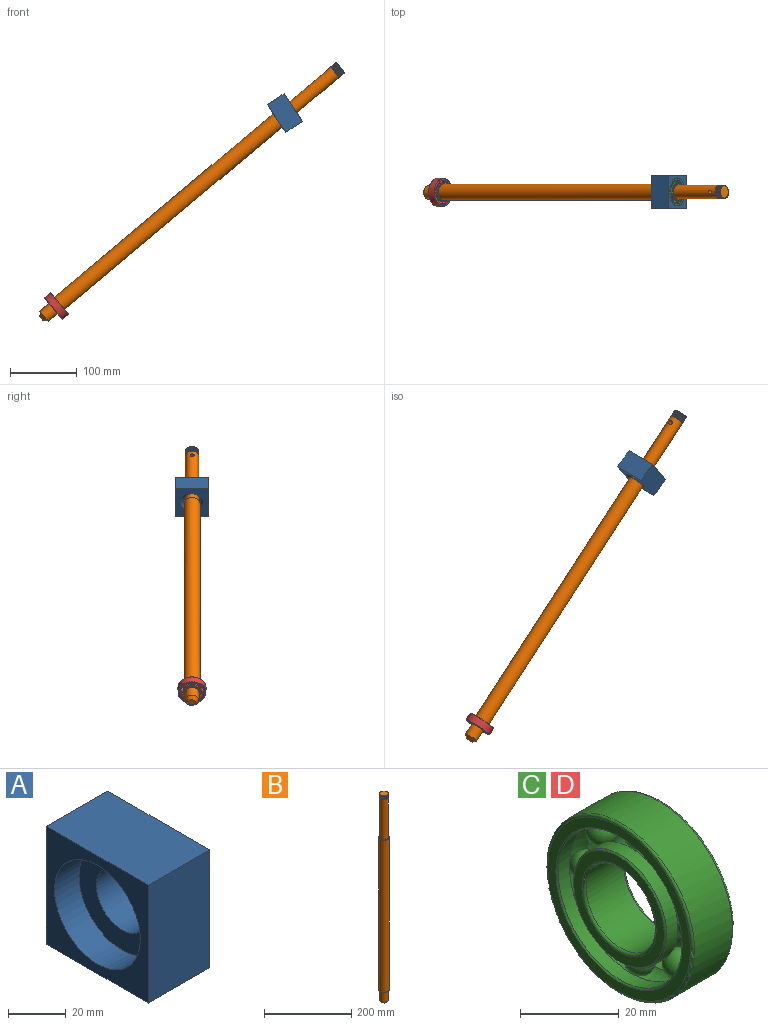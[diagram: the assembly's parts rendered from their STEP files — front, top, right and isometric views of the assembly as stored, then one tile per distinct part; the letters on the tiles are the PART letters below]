
ASSEMBLY  parts=4 mates=1
PART A: 10 faces, bbox 30x50x50 mm
  f0: plane 50x50mm, normal (-1,0,0), area 1114.6mm2, adj f1,f3,f4,f5,f8
  f1: plane 50x30mm, normal (0,-1,0), area 1500mm2, adj f0,f2,f4,f5
  f2: plane 50x50mm, normal (1,0,0), area 1537.9mm2, adj f1,f3,f4,f5,f9
  f3: plane 50x30mm, normal (0,1,0), area 1500mm2, adj f0,f2,f4,f5
  f4: plane 50x30mm, normal (0,0,1), area 1500mm2, adj f0,f1,f2,f3
  f5: plane 50x30mm, normal (0,0,-1), area 1500mm2, adj f0,f1,f2,f3
  f6: cylinder r=12.5mm len=25mm, axis (-1,0,0), area 1021mm2, adj f7,f9
  f7: plane 42x42mm, normal (-1,0,0), area 894.6mm2, adj f6,f8
  f8: cylinder r=21mm len=42mm, axis (-1,0,0), area 1583.4mm2, adj f0,f7
  f9: cone r=17.5mm half-angle=45deg, axis (1,0,0), area 666.4mm2, adj f2,f6
PART B: 27 faces, bbox 27.7x27.7x589.1 mm
  f0: plane 24x24mm, normal (0,0,-1), area 138.2mm2, adj f1,f2
  f1: cylinder r=10mm len=30mm, axis (0,0,-1), area 1885mm2, adj f0,f4
  f2: cylinder r=12mm len=427.31mm, axis (0,0,-1), area 32167.7mm2, adj f0,f5
  f3: plane 10x10mm, normal (0,0,-1), area 78.5mm2, adj f4
  f4: cone r=10mm half-angle=45deg, axis (0,0,1), area 333.2mm2, adj f1,f3
  f5: plane 27.66x27.66mm, normal (0,-0.11,0.99), area 139.1mm2, adj f2,f7
  f6: plane 19.73x19.68mm, normal (0,0,1), area 294.9mm2, adj f17,f21,f22,f23
  f7: cylinder r=10mm len=114.81mm, axis (0,0,-1), area 7046.2mm2, adj f5,f8,f18,f19,f20,f23,f25
  f8: cylinder r=10mm len=20mm, axis (0,0,-1), area 7.8mm2, adj f7,f9,f22,f23
  f9: cylinder r=10mm len=20mm, axis (0,0,-1), area 7.8mm2, adj f8,f10,f22,f23
  f10: cylinder r=10mm len=20mm, axis (0,0,-1), area 7.9mm2, adj f9,f11,f22,f23
  f11: cylinder r=10mm len=20mm, axis (0,0,-1), area 7.9mm2, adj f10,f12,f22,f23
  f12: cylinder r=10mm len=20mm, axis (0,0,-1), area 7.8mm2, adj f11,f13,f22,f23
  f13: cylinder r=10mm len=20mm, axis (0,0,-1), area 7.8mm2, adj f12,f14,f22,f23
  f14: cylinder r=10mm len=20mm, axis (0,0,-1), area 7.9mm2, adj f13,f15,f22,f23
  f15: cylinder r=10mm len=20mm, axis (0,0,-1), area 7.9mm2, adj f14,f16,f22,f23
  f16: cylinder r=10mm len=20mm, axis (0,0,-1), area 7.9mm2, adj f15,f17,f22,f23
  f17: cylinder r=10mm len=7.01mm, axis (0,0,-1), area 0.5mm2, adj f6,f16,f22
  f18: plane 0.3x0.1mm, normal (0,-1,0), area 0mm2, adj f7,f19,f20,f24
  f19: bspline ~20.83x20.66mm, area 20.8mm2, adj f7,f18,f22,f24
  f20: bspline ~20.83x20.66mm, area 20.7mm2, adj f7,f18,f23,f24
  f21: bspline ~21.84x18.92mm, area 158.5mm2, adj f6,f22,f23,f24
  f22: bspline ~23.09x20mm, area 354.5mm2, adj f6,f8,f9,f10,f11,f12,f13,f14
  f23: bspline ~23.09x20mm, area 375mm2, adj f6,f7,f8,f9,f10,f11,f12,f13
  f24: bspline ~19.74x19.57mm, area 17mm2, adj f18,f19,f20,f21
  f25: cylinder r=3mm len=10mm, axis (0,-1,0), area 188.4mm2, adj f7,f26
  f26: plane 6x6mm, normal (0,1,0), area 28.3mm2, adj f25
PART C: 42 faces, bbox 12x45.5x45.5 mm
  f0: plane 40.8x40.8mm, normal (-1,0,0), area 283.9mm2, adj f1,f18
  f1: torus R=20.4mm, axis (1,0,0), area 123.1mm2, adj f0,f2
  f2: cylinder r=21mm len=42mm, axis (1,0,0), area 1425mm2, adj f1,f3
  f3: torus R=20.4mm, axis (1,0,0), area 123.1mm2, adj f2,f4
  f4: plane 40.8x40.8mm, normal (1,0,0), area 283.9mm2, adj f3,f5
  f5: cone r=17.87mm half-angle=45deg, axis (1,0,0), area 55.5mm2, adj f4,f6
  f6: cylinder r=17.7mm len=35.4mm, axis (1,0,0), area 354.8mm2, adj f5,f7,f8,f9,f10,f11,f12,f13
  f7: sphere r=3.32mm, area 130.9mm2, adj f6,f11,f12,f17,f19,f27,f31,f32
  f8: torus R=15.5mm, axis (1,0,0), area 76.3mm2, adj f6,f16,f17,f36
  f9: torus R=15.5mm, axis (1,0,0), area 76.3mm2, adj f6,f16,f17,f38
  f10: torus R=15.5mm, axis (1,0,0), area 76.3mm2, adj f6,f17,f37,f38
  f11: torus R=15.5mm, axis (1,0,0), area 76.3mm2, adj f6,f7,f17,f37
  f12: torus R=15.5mm, axis (1,0,0), area 76.3mm2, adj f6,f7,f17,f39
  f13: torus R=15.5mm, axis (1,0,0), area 76.3mm2, adj f6,f17,f39,f40
  f14: torus R=15.5mm, axis (1,0,0), area 76.3mm2, adj f6,f17,f40,f41
  f15: torus R=15.5mm, axis (1,0,0), area 76.3mm2, adj f6,f17,f36,f41
  f16: sphere r=3.32mm, area 130.9mm2, adj f6,f8,f9,f17,f19,f27,f28,f29
  f17: cylinder r=17.7mm len=35.4mm, axis (1,0,0), area 354.8mm2, adj f7,f8,f9,f10,f11,f12,f13,f14
  f18: cone r=17.87mm half-angle=45deg, axis (-1,0,0), area 55.5mm2, adj f0,f17
  f19: cylinder r=13.3mm len=26.6mm, axis (1,0,0), area 266.6mm2, adj f7,f16,f20,f28,f29,f30,f31,f32
  f20: cone r=13.13mm half-angle=45deg, axis (1,0,0), area 40.8mm2, adj f19,f21
  f21: plane 25.9x25.9mm, normal (-1,0,0), area 173.9mm2, adj f20,f22
  f22: torus R=10.6mm, axis (1,0,0), area 60.5mm2, adj f21,f23
  f23: cylinder r=10mm len=20mm, axis (1,0,0), area 678.6mm2, adj f22,f24
  f24: torus R=10.6mm, axis (1,0,0), area 60.5mm2, adj f23,f25
  f25: plane 25.9x25.9mm, normal (1,0,0), area 173.9mm2, adj f24,f26
  f26: cone r=13.13mm half-angle=45deg, axis (-1,0,0), area 40.8mm2, adj f25,f27
  f27: cylinder r=13.3mm len=26.6mm, axis (1,0,0), area 266.6mm2, adj f7,f16,f26,f28,f29,f30,f31,f32
  f28: torus R=15.5mm, axis (1,0,0), area 51.5mm2, adj f16,f19,f27,f36
  f29: torus R=15.5mm, axis (1,0,0), area 51.5mm2, adj f16,f19,f27,f38
  f30: torus R=15.5mm, axis (1,0,0), area 51.5mm2, adj f19,f27,f37,f38
  f31: torus R=15.5mm, axis (1,0,0), area 51.5mm2, adj f7,f19,f27,f37
  f32: torus R=15.5mm, axis (1,0,0), area 51.5mm2, adj f7,f19,f27,f39
  f33: torus R=15.5mm, axis (1,0,0), area 51.5mm2, adj f19,f27,f39,f40
  f34: torus R=15.5mm, axis (1,0,0), area 51.5mm2, adj f19,f27,f40,f41
  f35: torus R=15.5mm, axis (1,0,0), area 51.5mm2, adj f19,f27,f36,f41
  f36: sphere r=3.32mm, area 130.9mm2, adj f6,f8,f15,f17,f19,f27,f28,f35
  f37: sphere r=3.32mm, area 130.9mm2, adj f6,f10,f11,f17,f19,f27,f30,f31
  f38: sphere r=3.32mm, area 130.9mm2, adj f6,f9,f10,f17,f19,f27,f29,f30
  f39: sphere r=3.32mm, area 130.9mm2, adj f6,f12,f13,f17,f19,f27,f32,f33
  f40: sphere r=3.32mm, area 130.9mm2, adj f6,f13,f14,f17,f19,f27,f33,f34
  f41: sphere r=3.32mm, area 130.9mm2, adj f6,f14,f15,f17,f19,f27,f34,f35
PART D: same geometry as C
PLACE A rot(axis=(-0.29,0,0.96),180deg) t=(204.56,0.09,267.37)mm
PLACE B rot(axis=(0.39,0.39,0.83),100.3deg) t=(-133.6,0.09,-18.14)mm
PLACE C rot(axis=(0,1,0),146.4deg) t=(212.06,0.09,272.35)mm
PLACE D rot(axis=(0,-1,0),40deg) t=(-138.19,0.09,-22)mm
MATE fastened C.f1 <-> A.f6  axis (-0.83,0,-0.55) through (207.06,0.09,269.03)mm
